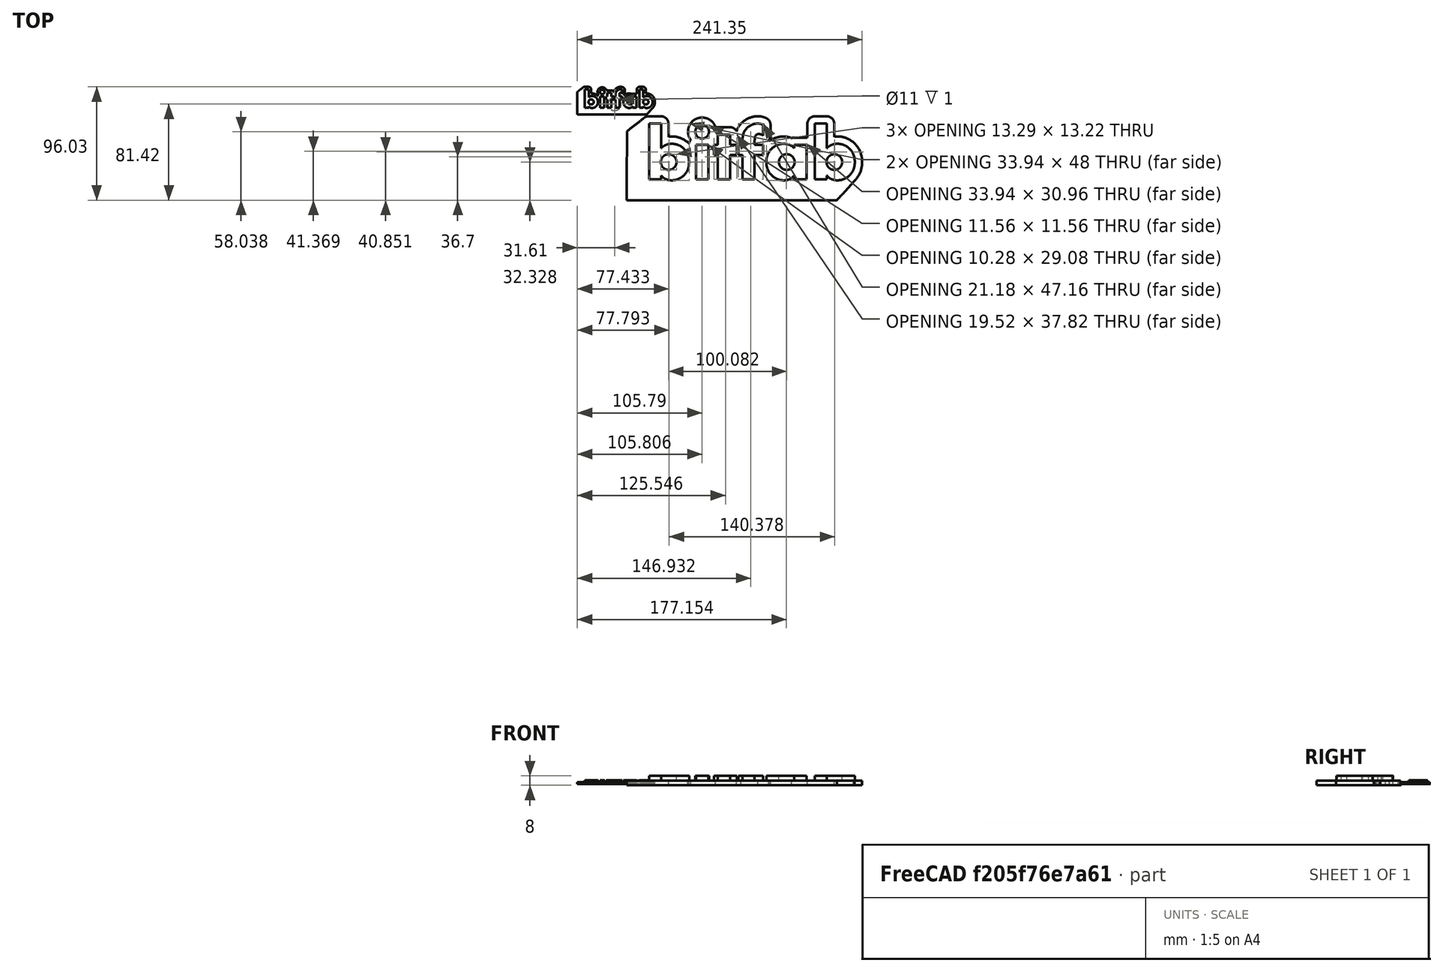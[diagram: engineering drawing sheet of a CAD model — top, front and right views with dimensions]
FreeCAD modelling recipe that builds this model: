
FCSTD DOCUMENT  (FreeCAD 0.16R6706 (Git))
Label: magnet_logo
License: All rights reserved
LicenseURL: http://en.wikipedia.org/wiki/All_rights_reserved
objects: Part::Feature×12, Part::Extrusion×11, Part::MultiFuse×3, Part::Cut×2, Part::FeaturePython×1, Part::Cylinder×1, Mesh::Feature×1
note: 30 computed .brp shape members not serialized (recipe doc carries the construction recipe); baked Part::Feature solids carry a one-line shape summary decoded from their .brp

FEATURE [Part::Feature] path4724
  shape: bbox 199.5 x 71.16 x 1.826e-06 mm, 0 faces, 0 solids (baked)
FEATURE [Part::Feature] path4146
  shape: bbox 33.94 x 48 x 1.826e-06 mm, 0 faces, 0 solids (baked)
FEATURE [Part::Feature] path4146001
  shape: bbox 13.29 x 13.22 x 1.826e-06 mm, 0 faces, 0 solids (baked)
FEATURE [Part::Feature] path4148
  shape: bbox 11.56 x 11.56 x 1.826e-06 mm, 0 faces, 0 solids (baked)
FEATURE [Part::Feature] path4148001
  shape: bbox 10.28 x 29.08 x 1.826e-06 mm, 0 faces, 0 solids (baked)
FEATURE [Part::Feature] path4150
  shape: bbox 19.52 x 37.82 x 1.826e-06 mm, 0 faces, 0 solids (baked)
FEATURE [Part::Feature] path4152
  shape: bbox 21.18 x 47.16 x 1.826e-06 mm, 0 faces, 0 solids (baked)
FEATURE [Part::Feature] path4154
  shape: bbox 33.94 x 30.96 x 1.826e-06 mm, 0 faces, 0 solids (baked)
FEATURE [Part::Feature] path4154001
  shape: bbox 13.29 x 13.22 x 1.826e-06 mm, 0 faces, 0 solids (baked)
FEATURE [Part::Feature] path4156
  shape: bbox 33.94 x 48 x 1.826e-06 mm, 0 faces, 0 solids (baked)
FEATURE [Part::Feature] path4156001
  shape: bbox 13.29 x 13.22 x 1.826e-06 mm, 0 faces, 0 solids (baked)
FEATURE [Part::Extrusion] Extrude
  Base = -> path4146
  Dir = (0,0,8)
  Solid = true
FEATURE [Part::Extrusion] Extrude001
  Base = -> path4148
  Dir = (0,0,8)
  Solid = true
FEATURE [Part::Extrusion] Extrude002
  Base = -> path4148001
  Dir = (0,0,8)
  Solid = true
FEATURE [Part::Extrusion] Extrude003
  Base = -> path4150
  Dir = (0,0,8)
  Solid = true
FEATURE [Part::Extrusion] Extrude004
  Base = -> path4152
  Dir = (0,0,8)
  Solid = true
FEATURE [Part::Extrusion] Extrude005
  Base = -> path4154
  Dir = (0,0,8)
  Solid = true
FEATURE [Part::Extrusion] Extrude006
  Base = -> path4156
  Dir = (0,0,8)
  Solid = true
FEATURE [Part::Extrusion] Extrude007
  Base = -> path4146001
  Dir = (0,0,8)
  Solid = true
FEATURE [Part::Extrusion] Extrude008
  Base = -> path4154001
  Dir = (0,0,8)
  Solid = true
FEATURE [Part::Extrusion] Extrude009
  Base = -> path4156001
  Dir = (0,0,8)
  Solid = true
FEATURE [Part::MultiFuse] Fusion  label="letters"
  Shapes = -> [Extrude,Extrude003,Extrude002,Extrude001,Extrude006,Extrude004,Extrude005]
FEATURE [Part::MultiFuse] Fusion001  label="holes"
  Shapes = -> [Extrude007,Extrude009,Extrude008]
FEATURE [Part::Extrusion] Extrude010  label="outline"
  Base = -> path4724
  Dir = (0,0,4)
  Solid = true
FEATURE [Part::Cut] Cut
  Base = -> Fusion
  Tool = -> Fusion001
FEATURE [Part::MultiFuse] Fusion002
  Shapes = -> [Extrude010,Cut]
FEATURE [Part::Feature] Fusion002004  label="Fusion006"
  shape: bbox 199.5 x 71.16 x 8 mm, 165 faces (baked)
FEATURE [Part::FeaturePython] Clone  label="Clone of Fusion006"  # Draft clone (typed FeaturePython)
  Objects = -> [Fusion002004]
  Placement = pos=(-35,18,1) rot=(0,0,1;0rad)
  Scale = (0.33,0.33,0.4)
FEATURE [Part::Cylinder] Cylinder
  Angle = 360
  Height = 2
  Radius = 5.5
FEATURE [Part::Cut] Cut001
  Base = -> Clone
  Tool = -> Cylinder
FEATURE [Mesh::Feature] Mesh  label="Cut001 (Meshed)"
